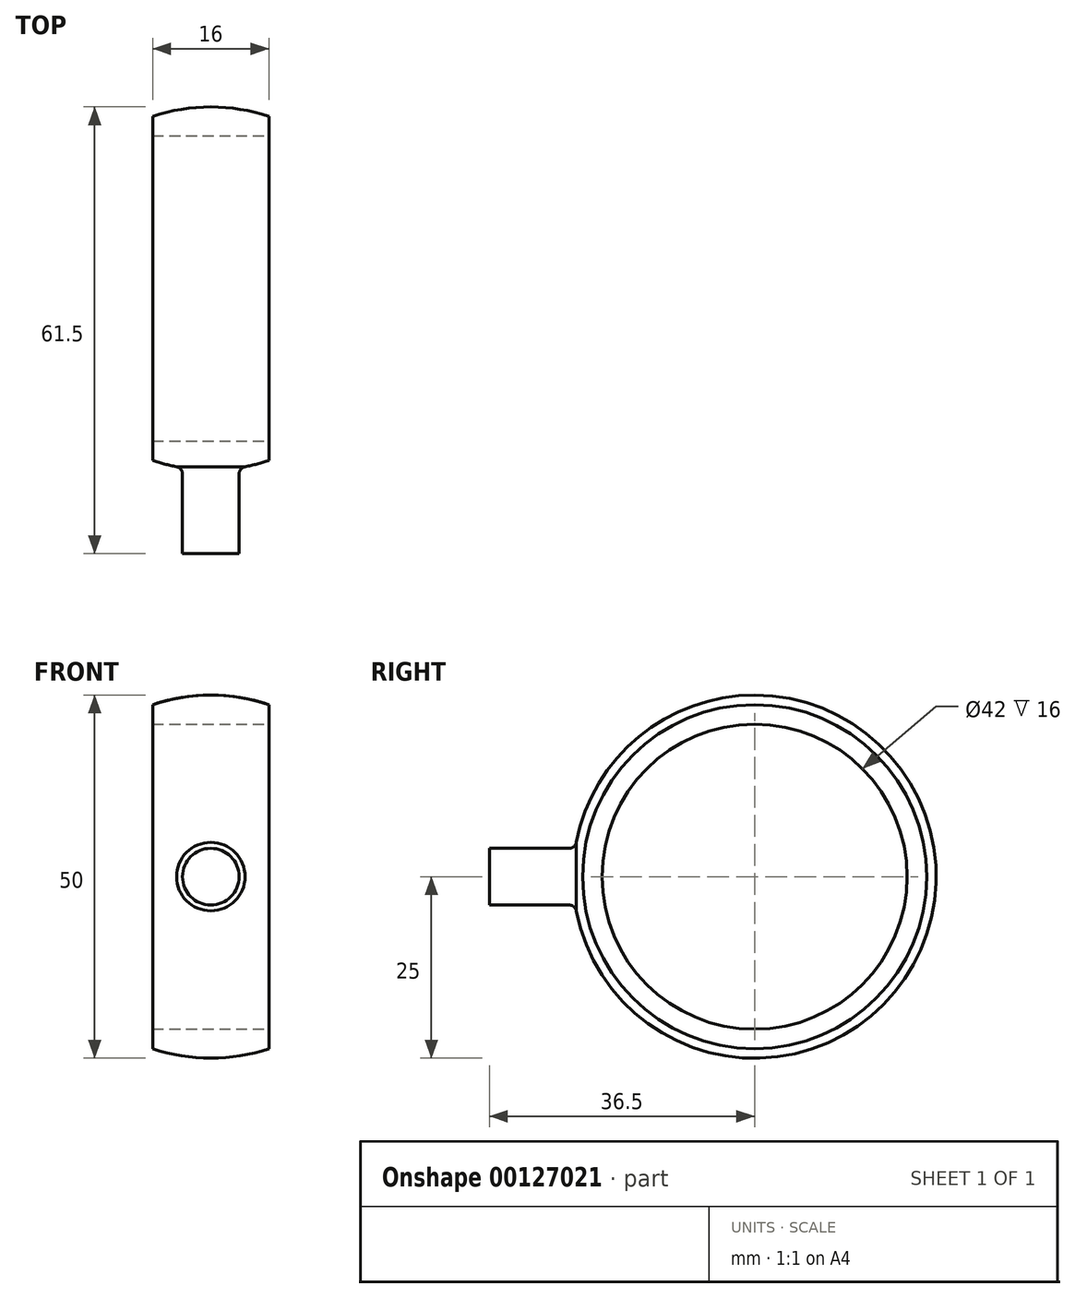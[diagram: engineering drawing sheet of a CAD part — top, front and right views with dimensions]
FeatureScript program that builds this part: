
annotation { "Feature Type Name" : "Feature", "Feature Type Description" : "" }
export const myFeature = defineFeature(function(context is Context, id is Id, definition is map)
    precondition{}
    {
        {
            var Q0;
            Q0=qCreatedBy(makeId("Front.planeOp"),FACE);
            var sketch = newSketch(context, id + "F0", { "sketchPlane" : qUnion([Q0])});
            skCircle(sketch, "E0", {"center": v(0, 0) * mm, "radius": 21 * mm});
            skCircle(sketch, "E1", {"center": v(0, 0) * mm, "radius": 25 * mm});
            skLineSegment(sketch, "E2", {"start": v(-25, 0) * mm, "end": v(25, 0) * mm});
            skSolve(sketch);
        }
        {
            var Q0;
            {var subQ0=sQuery(id+"F0.wireOp",EDGE,"E2");var subQ1=sQuery(id+"F0.wireOp",EDGE,"E0");var subQ2=makeQuery(id+"F0.imprint","INTERSECT",VERTEX,{"disambiguationData":[OD(0.0)],"derivedFrom":[subQ1,subQ0]});Q0=makeQuery(id+"F0.imprint","IMPRINT",FACE,{"disambiguationData":[TD([[makeQuery(id+"F0.imprint","IMPRINT",EDGE,{"disambiguationData":[TD([[subQ2,1.0]])],"derivedFrom":subQ1}),-1.0]])]});}
            var Q1;
            Q1=sQuery(id+"F0.wireOp",EDGE,"E2");
            revolve(context, id + "F1", {"entities" : qUnion([Q0]), "axis" : qUnion([Q1]), "revolveType" : RevolveType.FULL});
        }
        {
            var Q0;
            Q0=qCreatedBy(makeId("Front.planeOp"),FACE);
            var sketch = newSketch(context, id + "F2", { "sketchPlane" : qUnion([Q0])});
            skLineSegment(sketch, "E3.bottom", {"start": v(8, 43.57) * mm, "end": v(29.7, 43.57) * mm});
            skLineSegment(sketch, "E3.top", {"start": v(8, -44.34) * mm, "end": v(29.7, -44.34) * mm});
            skLineSegment(sketch, "E3.left", {"start": v(8, 43.57) * mm, "end": v(8, -44.34) * mm});
            skLineSegment(sketch, "E3.right", {"start": v(29.7, 43.57) * mm, "end": v(29.7, -44.34) * mm});
            skLineSegment(sketch, "E4.bottom", {"start": v(-8, 44.67) * mm, "end": v(-32.28, 44.67) * mm});
            skLineSegment(sketch, "E4.top", {"start": v(-8, -49.49) * mm, "end": v(-32.28, -49.49) * mm});
            skLineSegment(sketch, "E4.left", {"start": v(-8, 44.67) * mm, "end": v(-8, -49.49) * mm});
            skLineSegment(sketch, "E4.right", {"start": v(-32.28, 44.67) * mm, "end": v(-32.28, -49.49) * mm});
            skSolve(sketch);
        }
        {
            var Q0;
            Q0 = qSketchRegion(id + "F2", true);
            extrude(context, id + "F3", {"entities" : qUnion([Q0]), "operationType" : NewBodyOperationType.REMOVE, "endBound" : BoundingType.SYMMETRIC, "oppositeDirection" : true, "depth" : 60 * mm});
        }
        {
            var Q0;
            Q0=makeQuery(id+"F3.boolean.opBoolean","COPY",FACE,{"derivedFrom":makeQuery(id+"F3.opExtrude","SWEPT_FACE",FACE,{"disambiguationData":[OSD([sQuery(id+"F2.wireOp",EDGE,"E3.left")])]})});
            var sketch = newSketch(context, id + "F4", { "sketchPlane" : qUnion([Q0])});
            skCircle(sketch, "E5", {"center": v(0, 0) * mm, "radius": 20 * mm});
            skSolve(sketch);
        }
        {
            var Q0;
            Q0 = qSketchRegion(id + "F4", true);
            extrude(context, id + "F5", {"entities" : qUnion([Q0]), "operationType" : NewBodyOperationType.REMOVE, "oppositeDirection" : true, "depth" : 15 * mm});
        }
        {
            var Q0;
            Q0=makeQuery(id+"F3.boolean.opBoolean","COPY",FACE,{"derivedFrom":makeQuery(id+"F3.opExtrude","SWEPT_FACE",FACE,{"disambiguationData":[OSD([sQuery(id+"F2.wireOp",EDGE,"E3.left")])]})});
            var sketch = newSketch(context, id + "F6", { "sketchPlane" : qUnion([Q0])});
            skCircle(sketch, "E6", {"center": v(0, 0) * mm, "radius": 21 * mm});
            skSolve(sketch);
        }
        {
            var Q0;
            Q0 = qSketchRegion(id + "F6", true);
            extrude(context, id + "F7", {"entities" : qUnion([Q0]), "operationType" : NewBodyOperationType.REMOVE, "endBound" : BoundingType.SYMMETRIC, "oppositeDirection" : true, "depth" : 60 * mm});
        }
        {
            var Q0;
            Q0=qCreatedBy(makeId("Front.planeOp"),FACE);
            cPlane(context, id + "F8", {"entities" : qUnion([Q0]), "cplaneType" : CPlaneType.OFFSET, "offset" : 25 * mm, "width" : 150 * mm, "height" : 150 * mm});
        }
        {
            var Q0;
            Q0=qCreatedBy(id+"F8.planeOp",FACE);
            var sketch = newSketch(context, id + "F9", { "sketchPlane" : qUnion([Q0])});
            skCircle(sketch, "E7", {"center": v(0, 0) * mm, "radius": 3.9 * mm});
            skSolve(sketch);
        }
        {
            var Q0;
            Q0 = qSketchRegion(id + "F9", true);
            extrude(context, id + "F10", {"entities" : qUnion([Q0]), "endBound" : BoundingType.SYMMETRIC, "depth" : 3 * mm});
        }
        {
            var Q0;
            Q0=makeQuery(id+"F10.opExtrude","CAP_FACE",FACE,{"disambiguationData":[OSD([sQuery(id+"F9.wireOp",EDGE,"E7")])],"isStart":false});
            extrude(context, id + "F11", {"entities" : qUnion([Q0]), "operationType" : NewBodyOperationType.ADD, "depth" : 10 * mm});
        }
        {
            var Q0;
            Q0=makeQuery(id+"F10.opExtrude","SWEPT_BODY",BODY,{"disambiguationData":[OSD([sQuery(id+"F9.wireOp",EDGE,"E7")])]});
            var Q1;
            Q1=makeQuery(id+"F1.opRevolve","SWEPT_BODY",BODY,{"disambiguationData":[OSD([sQuery(id+"F0.wireOp",EDGE,"E0"),sQuery(id+"F0.wireOp",EDGE,"E1"),sQuery(id+"F0.wireOp",EDGE,"E2")])]});
            booleanBodies(context, id + "F12", {"operationType" : BooleanOperationType.UNION, "tools" : qUnion([Q0, Q1])});
        }
        {
            var Q0;
            {var subQ0=sQuery(id+"F9.wireOp",EDGE,"E7");Q0=makeQuery(id+"F12.opBoolean","INTERSECT",EDGE,{"derivedFrom":[makeQuery(id+"F1.opRevolve","SWEPT_FACE",FACE,{"disambiguationData":[OSD([sQuery(id+"F0.wireOp",EDGE,"E1")])]}),makeQuery(id+"F11.boolean.opBoolean","MERGE",FACE,{"derivedFrom":[makeQuery(id+"F10.opExtrude","SWEPT_FACE",FACE,{"disambiguationData":[OSD([subQ0])]}),makeQuery(id+"F11.opExtrude","SWEPT_FACE",FACE,{"disambiguationData":[OSD([subQ0])]})]})]});}
            fillet(context, id + "F13", {"entities" : qUnion([Q0]), "radius" : 1 * mm, "tangentPropagation" : true, "allowEdgeOverflow" : false});
        }
    });
